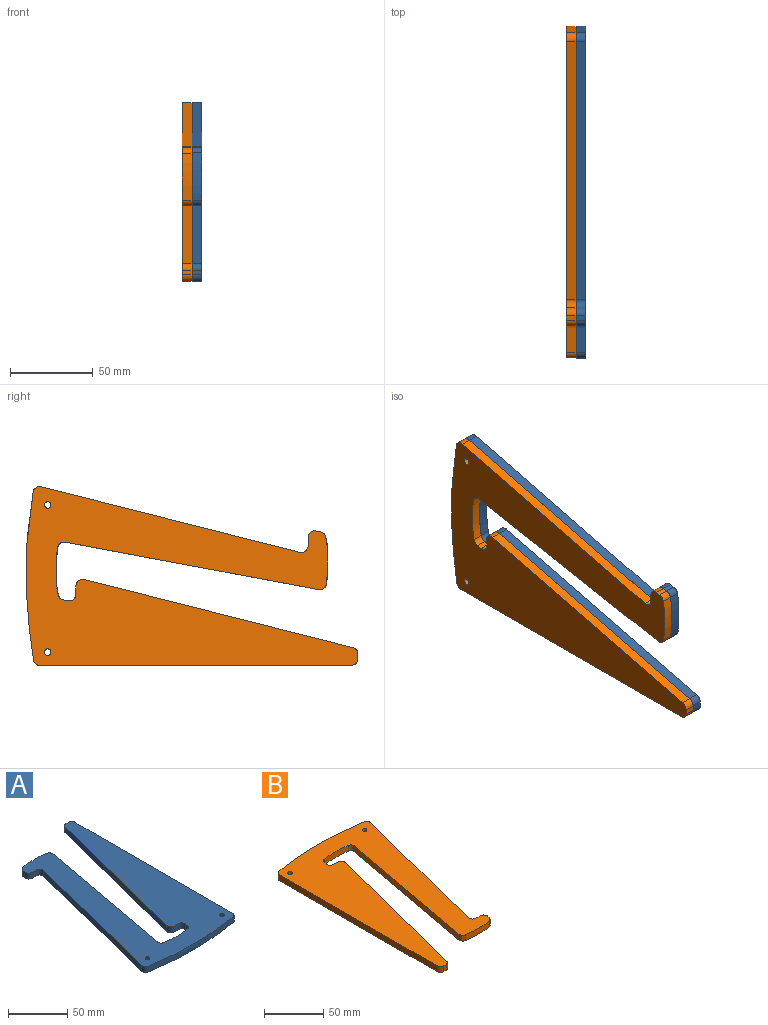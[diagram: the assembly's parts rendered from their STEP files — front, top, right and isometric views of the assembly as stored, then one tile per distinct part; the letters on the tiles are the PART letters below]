
ASSEMBLY  parts=2 mates=1
PART A: 28 faces, bbox 107.8x200.3x6 mm
  f0: plane 155.87x39.48mm, normal (-0.97,0.25,0), area 964.8mm2, adj f14,f15,f16,f27
  f1: extruded ~101.1x6mm, area 609.5mm2, adj f14,f15,f16,f17
  f2: plane 187.57x6mm, normal (1,0,0), area 1125.4mm2, adj f14,f15,f17,f18
  f3: plane 6x2.89mm, normal (0,1,0), area 17.3mm2, adj f14,f15,f18,f19
  f4: plane 162x41.03mm, normal (-0.97,0.25,0), area 1002.7mm2, adj f14,f15,f19,f20
  f5: plane 6x5.01mm, normal (0,-1,0), area 30mm2, adj f14,f15,f20,f21
  f6: plane 6x2.67mm, normal (-0.98,0.19,0), area 16.3mm2, adj f14,f15,f21,f22
  f7: extruded ~28.43x6mm, area 171.6mm2, adj f14,f15,f22,f23
  f8: plane 152.48x28.59mm, normal (0.98,-0.18,0), area 930.8mm2, adj f14,f15,f23,f24
  f9: extruded ~28.63x6mm, area 172.7mm2, adj f14,f15,f24,f25
  f10: plane 6x2.8mm, normal (-0.98,0.19,0), area 17.1mm2, adj f14,f15,f25,f26
  f11: cylinder r=2mm len=6mm, axis (0,0,-1), area 75.4mm2, adj f14,f15
  f12: cylinder r=2mm len=6mm, axis (0,0,-1), area 75.4mm2, adj f14,f15
  f13: plane 6x5.01mm, normal (0,-1,0), area 30mm2, adj f14,f15,f26,f27
  f14: plane 200.26x107.81mm, normal (0,0,1), area 11777.4mm2, adj f0,f1,f2,f3,f4,f5,f6,f7
  f15: plane 200.26x107.81mm, normal (0,0,-1), area 11777.4mm2, adj f0,f1,f2,f3,f4,f5,f6,f7
  f16: cylinder r=4mm len=6mm, axis (0,0,-1), area 39.5mm2, adj f0,f1,f14,f15
  f17: cylinder r=4mm len=6mm, axis (0,0,-1), area 34.1mm2, adj f1,f2,f14,f15
  f18: cylinder r=4mm len=6mm, axis (0,0,-1), area 37.7mm2, adj f2,f3,f14,f15
  f19: cylinder r=4mm len=6mm, axis (0,0,1), area 31.7mm2, adj f3,f4,f14,f15
  f20: cylinder r=4mm len=6mm, axis (0,0,1), area 43.7mm2, adj f4,f5,f14,f15
  f21: cylinder r=4mm len=6mm, axis (0,0,1), area 42.3mm2, adj f5,f6,f14,f15
  f22: cylinder r=4mm len=6mm, axis (0,0,-1), area 28.3mm2, adj f6,f7,f14,f15
  f23: cylinder r=4mm len=6mm, axis (0,0,-1), area 37.8mm2, adj f7,f8,f14,f15
  f24: cylinder r=4mm len=6mm, axis (0,0,-1), area 37.4mm2, adj f8,f9,f14,f15
  f25: cylinder r=4mm len=6mm, axis (0,0,-1), area 27.5mm2, adj f9,f10,f14,f15
  f26: cylinder r=4mm len=6mm, axis (0,0,-1), area 42.3mm2, adj f10,f13,f14,f15
  f27: cylinder r=4mm len=6mm, axis (0,0,1), area 43.7mm2, adj f0,f13,f14,f15
PART B: 28 faces, bbox 107.8x200.3x6 mm
  f0: plane 155.86x39.48mm, normal (0.97,-0.25,0), area 964.7mm2, adj f14,f15,f16,f27
  f1: extruded ~101.12x6mm, area 609.7mm2, adj f14,f15,f16,f17
  f2: plane 187.6x6mm, normal (-1,0,0), area 1125.6mm2, adj f14,f15,f17,f18
  f3: plane 6x2.89mm, normal (0,-1,0), area 17.3mm2, adj f14,f15,f18,f19
  f4: plane 162x41.03mm, normal (0.97,-0.25,0), area 1002.7mm2, adj f14,f15,f19,f20
  f5: plane 6x5.01mm, normal (0,1,0), area 30mm2, adj f14,f15,f20,f21
  f6: plane 6x2.8mm, normal (0.98,-0.19,0), area 17.1mm2, adj f14,f15,f21,f22
  f7: extruded ~28.63x6mm, area 172.7mm2, adj f14,f15,f22,f23
  f8: plane 152.48x28.59mm, normal (-0.98,0.18,0), area 930.8mm2, adj f14,f15,f23,f24
  f9: extruded ~28.43x6mm, area 171.6mm2, adj f14,f15,f24,f25
  f10: plane 6x2.67mm, normal (0.98,-0.19,0), area 16.3mm2, adj f14,f15,f25,f26
  f11: cylinder r=2mm len=6mm, axis (0,0,-1), area 75.4mm2, adj f14,f15
  f12: cylinder r=2mm len=6mm, axis (0,0,-1), area 75.4mm2, adj f14,f15
  f13: plane 6x5.01mm, normal (0,1,0), area 30mm2, adj f14,f15,f26,f27
  f14: plane 200.26x107.8mm, normal (0,0,1), area 11773.2mm2, adj f0,f1,f2,f3,f4,f5,f6,f7
  f15: plane 200.26x107.8mm, normal (0,0,-1), area 11773.2mm2, adj f0,f1,f2,f3,f4,f5,f6,f7
  f16: cylinder r=4mm len=6mm, axis (0,0,-1), area 39.5mm2, adj f0,f1,f14,f15
  f17: cylinder r=4mm len=6mm, axis (0,0,-1), area 33.9mm2, adj f1,f2,f14,f15
  f18: cylinder r=4mm len=6mm, axis (0,0,1), area 37.7mm2, adj f2,f3,f14,f15
  f19: cylinder r=4mm len=6mm, axis (0,0,-1), area 31.7mm2, adj f3,f4,f14,f15
  f20: cylinder r=4mm len=6mm, axis (0,0,-1), area 43.7mm2, adj f4,f5,f14,f15
  f21: cylinder r=4mm len=6mm, axis (0,0,1), area 42.3mm2, adj f5,f6,f14,f15
  f22: cylinder r=4mm len=6mm, axis (0,0,-1), area 27.5mm2, adj f6,f7,f14,f15
  f23: cylinder r=4mm len=6mm, axis (0,0,-1), area 37.4mm2, adj f7,f8,f14,f15
  f24: cylinder r=4mm len=6mm, axis (0,0,-1), area 37.8mm2, adj f8,f9,f14,f15
  f25: cylinder r=4mm len=6mm, axis (0,0,-1), area 28.3mm2, adj f9,f10,f14,f15
  f26: cylinder r=4mm len=6mm, axis (0,0,-1), area 42.3mm2, adj f10,f13,f14,f15
  f27: cylinder r=4mm len=6mm, axis (0,0,-1), area 43.7mm2, adj f0,f13,f14,f15
PLACE A rot(axis=(-0.71,0,0.71),180deg) t=(-69.16,-11.53,12.22)mm
PLACE B rot(axis=(0,-1,0),90deg) t=(-75.16,-26.51,90.38)mm
MATE fastened A.f16 <-> B.f16  axis (-1,0,0) through (-75.16,72.81,95.1)mm
